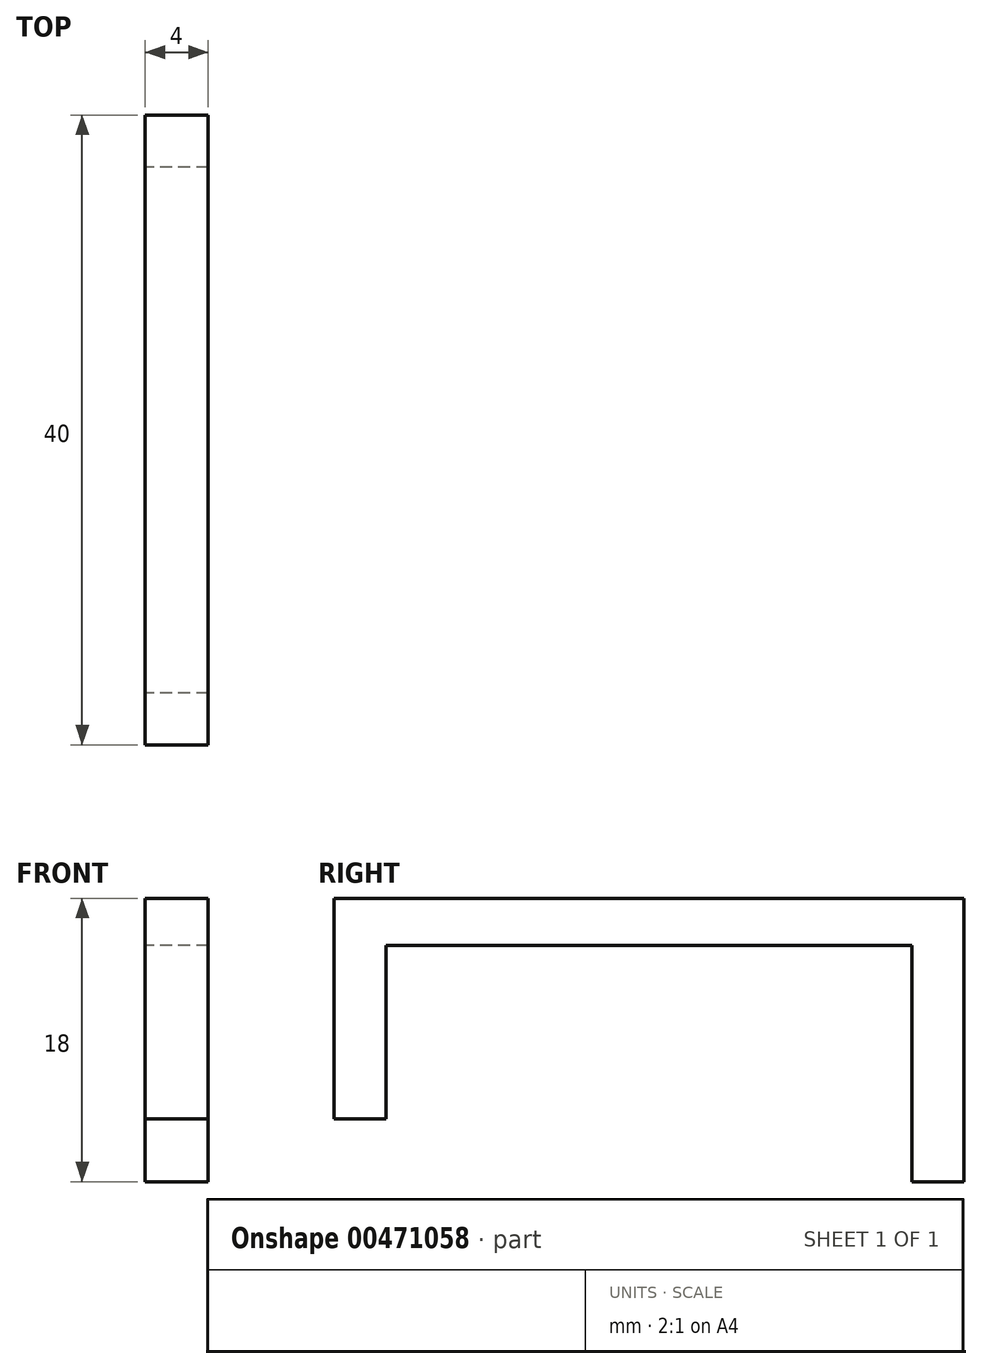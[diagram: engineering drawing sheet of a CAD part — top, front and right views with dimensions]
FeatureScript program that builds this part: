
annotation { "Feature Type Name" : "Feature", "Feature Type Description" : "" }
export const myFeature = defineFeature(function(context is Context, id is Id, definition is map)
    precondition{}
    {
        {
            var Q0;
            Q0=qCreatedBy(makeId("Right.planeOp"),FACE);
            var sketch = newSketch(context, id + "F0", { "sketchPlane" : qUnion([Q0])});
            skLineSegment(sketch, "E0", {"start": v(-89.2, -39.18) * mm, "end": v(-89.2, -25.18) * mm});
            skLineSegment(sketch, "E1", {"start": v(-89.2, -25.18) * mm, "end": v(-49.2, -25.18) * mm});
            skLineSegment(sketch, "E2", {"start": v(-52.5, -28.18) * mm, "end": v(-85.9, -28.18) * mm});
            skLineSegment(sketch, "E3", {"start": v(-85.9, -28.18) * mm, "end": v(-85.9, -39.18) * mm});
            skLineSegment(sketch, "E4", {"start": v(-85.9, -39.18) * mm, "end": v(-89.2, -39.18) * mm});
            skLineSegment(sketch, "E5", {"start": v(-49.2, -25.18) * mm, "end": v(-49.2, -43.18) * mm});
            skLineSegment(sketch, "E6", {"start": v(-52.5, -28.18) * mm, "end": v(-52.5, -43.18) * mm});
            skLineSegment(sketch, "E7", {"start": v(-52.5, -43.18) * mm, "end": v(-49.2, -43.18) * mm});
            skSolve(sketch);
        }
        {
            var Q0;
            Q0 = qSketchRegion(id + "F0", true);
            extrude(context, id + "F1", {"entities" : qUnion([Q0]), "depth" : 4 * mm, "offsetDistance" : 25 * mm});
        }
    });
